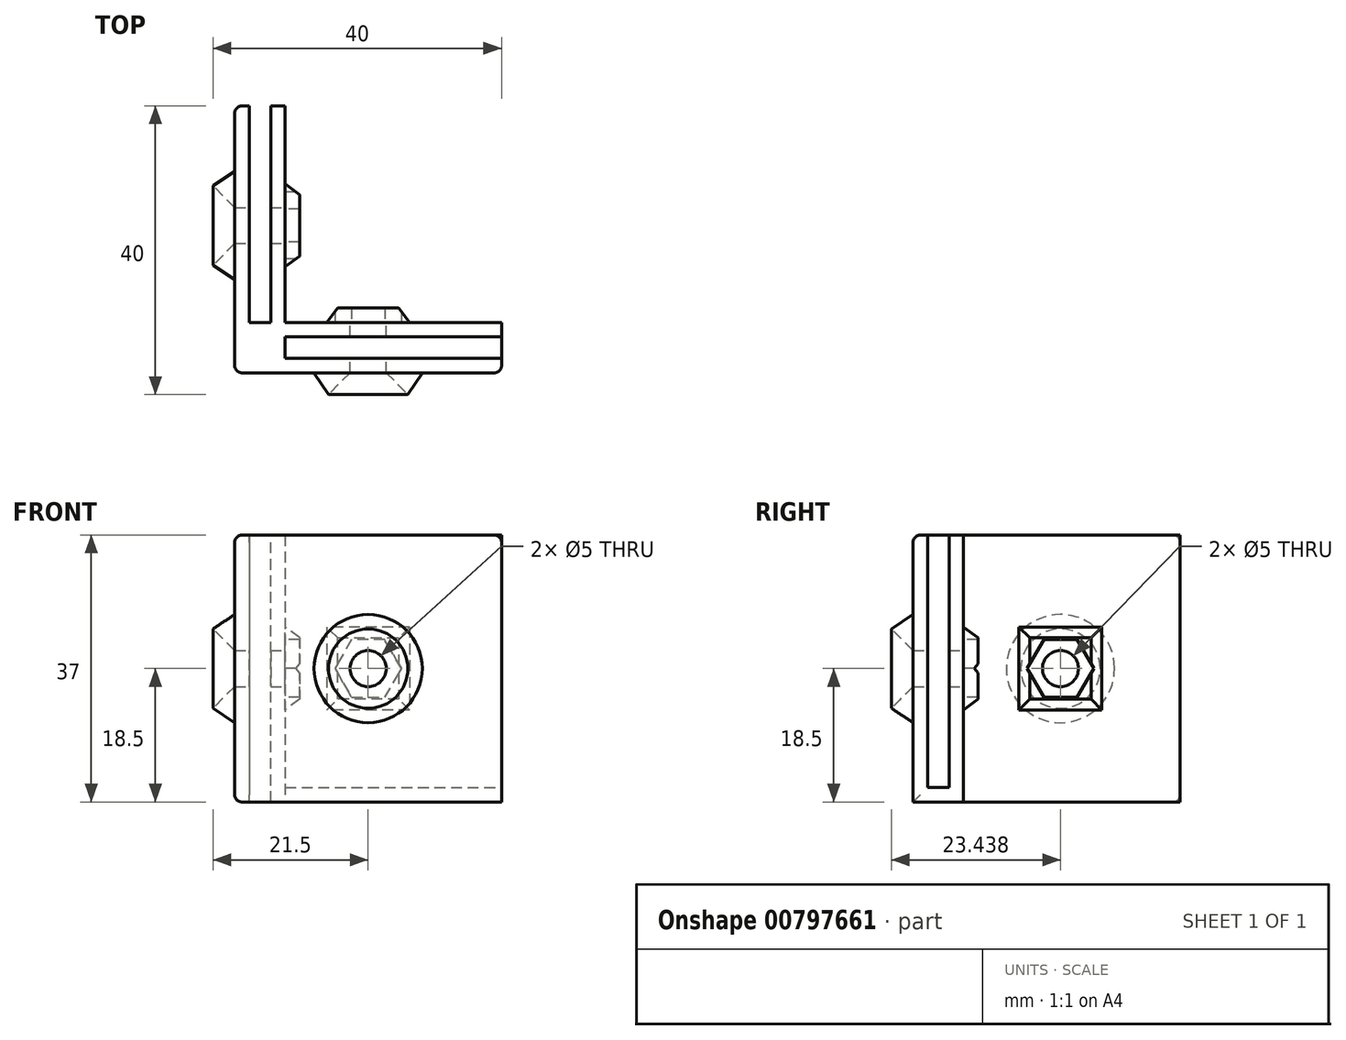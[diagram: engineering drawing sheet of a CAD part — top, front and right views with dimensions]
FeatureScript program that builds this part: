
annotation { "Feature Type Name" : "Feature", "Feature Type Description" : "" }
export const myFeature = defineFeature(function(context is Context, id is Id, definition is map)
    precondition{}
    {
        {
            var Q0;
            Q0=qCreatedBy(makeId("Front.planeOp"),FACE);
            var sketch = newSketch(context, id + "F0", { "sketchPlane" : qUnion([Q0])});
            skLineSegment(sketch, "E0.bottom", {"start": v(18.5, 18.5) * mm, "end": v(-18.5, 18.5) * mm});
            skLineSegment(sketch, "E0.top", {"start": v(18.5, -18.5) * mm, "end": v(-18.5, -18.5) * mm});
            skLineSegment(sketch, "E0.left", {"start": v(18.5, 18.5) * mm, "end": v(18.5, -18.5) * mm});
            skLineSegment(sketch, "E0.right", {"start": v(-18.5, 18.5) * mm, "end": v(-18.5, -18.5) * mm});
            skPoint(sketch, "E0.middle", {"position": v(0, 0) * mm});
            skSolve(sketch);
        }
        {
            var Q0;
            Q0=makeQuery(id+"F0.imprint","IMPRINT",FACE,{"disambiguationData":[TD([[makeQuery(id+"F0.imprint","IMPRINT",EDGE,{"derivedFrom":sQuery(id+"F0.wireOp",EDGE,"E0.bottom")}),1.0]])]});
            extrude(context, id + "F1", {"entities" : qUnion([Q0]), "depth" : 37 * mm, "offsetDistance" : 25 * mm});
        }
        {
            var Q0;
            Q0=makeQuery(id+"F1.opExtrude","CAP_FACE",FACE,{"disambiguationData":[OSD([sQuery(id+"F0.wireOp",EDGE,"E0.bottom"),sQuery(id+"F0.wireOp",EDGE,"E0.top"),sQuery(id+"F0.wireOp",EDGE,"E0.left"),sQuery(id+"F0.wireOp",EDGE,"E0.right")])],"isStart":true});
            var sketch = newSketch(context, id + "F2", { "sketchPlane" : qUnion([Q0])});
            skLineSegment(sketch, "E1", {"start": v(18.5, 18.5) * mm, "end": v(16.5, 18.5) * mm});
            skLineSegment(sketch, "E2", {"start": v(16.5, 18.5) * mm, "end": v(16.5, -16.5) * mm});
            skLineSegment(sketch, "E3", {"start": v(16.5, -16.5) * mm, "end": v(16.5, -18.5) * mm});
            skLineSegment(sketch, "E4", {"start": v(16.5, -18.5) * mm, "end": v(13.5, -18.5) * mm});
            skLineSegment(sketch, "E5", {"start": v(13.5, -18.5) * mm, "end": v(13.5, 18.5) * mm});
            skLineSegment(sketch, "E6", {"start": v(13.5, 18.5) * mm, "end": v(11.5, 18.5) * mm});
            skLineSegment(sketch, "E7", {"start": v(11.5, 18.5) * mm, "end": v(11.5, -18.5) * mm});
            skSolve(sketch);
        }
        {
            var Q0;
            Q0 = qSketchRegion(id + "F2", true);
            var Q1;
            {var subQ0=sQuery(id+"F2.wireOp",EDGE,"E7");Q1=makeQuery(id+"F2.imprint","IMPRINT",FACE,{"disambiguationData":[TD([[makeQuery(id+"F2.imprint","IMPRINT",EDGE,{"derivedFrom":subQ0}),-1.0]])]});}
            var Q2;
            {var subQ1=sQuery(id+"F2.wireOp",EDGE,"E2");Q2=makeQuery(id+"F2.imprint","IMPRINT",FACE,{"disambiguationData":[TD([[makeQuery(id+"F2.imprint","IMPRINT",EDGE,{"derivedFrom":subQ1}),-1.0]])]});}
            extrude(context, id + "F3", {"entities" : qUnion([Q0, Q1, Q2]), "operationType" : NewBodyOperationType.REMOVE, "oppositeDirection" : true, "depth" : 30 * mm, "offsetDistance" : 25 * mm});
        }
        {
            var Q0;
            Q0=makeQuery(id+"F1.opExtrude","SWEPT_FACE",FACE,{"disambiguationData":[OSD([sQuery(id+"F0.wireOp",EDGE,"E0.left")])]});
            var sketch = newSketch(context, id + "F4", { "sketchPlane" : qUnion([Q0])});
            skLineSegment(sketch, "E8", {"start": v(-37, 18.5) * mm, "end": v(-35, 18.5) * mm});
            skLineSegment(sketch, "E9", {"start": v(-35, 18.5) * mm, "end": v(-35, -16.5) * mm});
            skLineSegment(sketch, "E10", {"start": v(-35, -16.5) * mm, "end": v(-32, -16.5) * mm});
            skLineSegment(sketch, "E11", {"start": v(-32, -16.5) * mm, "end": v(-32, 18.5) * mm});
            skSolve(sketch);
        }
        {
            var Q0;
            Q0 = qSketchRegion(id + "F4", true);
            var Q1;
            {var subQ0=sQuery(id+"F4.wireOp",EDGE,"E9");Q1=makeQuery(id+"F4.imprint","IMPRINT",FACE,{"disambiguationData":[TD([[makeQuery(id+"F4.imprint","IMPRINT",EDGE,{"derivedFrom":subQ0}),1.0]])]});}
            extrude(context, id + "F5", {"entities" : qUnion([Q0, Q1]), "operationType" : NewBodyOperationType.REMOVE, "oppositeDirection" : true, "depth" : 30 * mm, "offsetDistance" : 25 * mm});
        }
        {
            var Q0;
            Q0=makeQuery(id+"F1.opExtrude","CAP_EDGE",EDGE,{"disambiguationData":[OSD([sQuery(id+"F0.wireOp",EDGE,"E0.right")])],"isStart":false});
            var Q1;
            Q1=makeQuery(id+"F1.opExtrude","SWEPT_EDGE",EDGE,{"disambiguationData":[OSD([sQuery(id+"F0.wireOp",EDGE,"E0.bottom"),sQuery(id+"F0.wireOp",EDGE,"E0.right")])]});
            var Q2;
            Q2=makeQuery(id+"F3.boolean.opBoolean","COPY",EDGE,{"derivedFrom":makeQuery(id+"F3.opExtrude","SWEPT_EDGE",EDGE,{"disambiguationData":[OSD([sQuery(id+"F0.wireOp",EDGE,"E0.bottom"),sQuery(id+"F2.wireOp",EDGE,"E6"),sQuery(id+"F2.wireOp",EDGE,"E7")])]})});
            var Q3;
            Q3=makeQuery(id+"F1.opExtrude","SWEPT_EDGE",EDGE,{"disambiguationData":[OSD([sQuery(id+"F0.wireOp",EDGE,"E0.top"),sQuery(id+"F0.wireOp",EDGE,"E0.right")])]});
            var Q4;
            Q4=makeQuery(id+"F3.boolean.opBoolean","COPY",EDGE,{"derivedFrom":makeQuery(id+"F3.opExtrude","SWEPT_EDGE",EDGE,{"disambiguationData":[OSD([sQuery(id+"F0.wireOp",EDGE,"E0.top"),sQuery(id+"F2.wireOp",EDGE,"E7")])]})});
            var Q5;
            Q5=makeQuery(id+"F1.opExtrude","CAP_EDGE",EDGE,{"disambiguationData":[OSD([sQuery(id+"F0.wireOp",EDGE,"E0.left")])],"isStart":false});
            var Q6;
            Q6=makeQuery(id+"F3.boolean.opBoolean","COPY",EDGE,{"derivedFrom":makeQuery(id+"F3.opExtrude","CAP_EDGE",EDGE,{"disambiguationData":[OSD([sQuery(id+"F0.wireOp",EDGE,"E0.left")])],"isStart":false})});
            fillet(context, id + "F6", {"entities" : qUnion([Q0, Q1, Q2, Q3, Q4, Q5, Q6]), "radius" : 1 * mm, "tangentPropagation" : true, "allowEdgeOverflow" : false});
        }
        {
            var Q0;
            Q0=makeQuery(id+"F3.boolean.opBoolean","COPY",FACE,{"derivedFrom":makeQuery(id+"F3.opExtrude","CAP_FACE",FACE,{"disambiguationData":[OSD([sQuery(id+"F0.wireOp",EDGE,"E0.bottom"),sQuery(id+"F0.wireOp",EDGE,"E0.top"),sQuery(id+"F0.wireOp",EDGE,"E0.left"),sQuery(id+"F2.wireOp",EDGE,"E7")])],"isStart":false})});
            var sketch = newSketch(context, id + "F7", { "sketchPlane" : qUnion([Q0])});
            skCircle(sketch, "E12", {"center": v(0, 0) * mm, "radius": 2.5 * mm});
            skLineSegment(sketch, "E13.bottom", {"start": v(-5.75, 5.75) * mm, "end": v(5.75, 5.75) * mm});
            skLineSegment(sketch, "E13.top", {"start": v(-5.75, -5.75) * mm, "end": v(5.75, -5.75) * mm});
            skLineSegment(sketch, "E13.left", {"start": v(-5.75, 5.75) * mm, "end": v(-5.75, -5.75) * mm});
            skLineSegment(sketch, "E13.right", {"start": v(5.75, 5.75) * mm, "end": v(5.75, -5.75) * mm});
            skCircle(sketch, "E14.cCircle", {"center": v(0, 0) * mm, "radius": 4 * mm, "construction": true});
            skPoint(sketch, "E14.cCircle.perimeterSnap0", {"position": v(0, 5.75) * mm});
            skLineSegment(sketch, "E14.0", {"start": v(-2.3, 4) * mm, "end": v(2.3, 4) * mm});
            skLineSegment(sketch, "E14.1", {"start": v(2.3, 4) * mm, "end": v(4.62, 0) * mm});
            skLineSegment(sketch, "E14.2", {"start": v(4.62, 0) * mm, "end": v(2.3, -4) * mm});
            skLineSegment(sketch, "E14.3", {"start": v(2.3, -4) * mm, "end": v(-2.3, -4) * mm});
            skLineSegment(sketch, "E14.4", {"start": v(-2.3, -4) * mm, "end": v(-4.62, 0) * mm});
            skLineSegment(sketch, "E14.5", {"start": v(-4.62, 0) * mm, "end": v(-2.3, 4) * mm});
            skPoint(sketch, "E14.0.midPoint", {"position": v(0, 4) * mm});
            skPoint(sketch, "E14.0.midPoint.positionSnap0", {"position": v(0, 5.75) * mm});
            skSolve(sketch);
        }
        {
            var Q0;
            Q0=makeQuery(id+"F7.imprint","IMPRINT",FACE,{"disambiguationData":[TD([[makeQuery(id+"F7.imprint","IMPRINT",EDGE,{"derivedFrom":sQuery(id+"F7.wireOp",EDGE,"E13.bottom")}),-1.0]])]});
            extrude(context, id + "F8", {"entities" : qUnion([Q0]), "operationType" : NewBodyOperationType.ADD, "depth" : 2 * mm, "offsetDistance" : 25 * mm});
        }
        {
            var Q0;
            Q0=makeQuery(id+"F7.imprint","IMPRINT",FACE,{"disambiguationData":[TD([[makeQuery(id+"F7.imprint","IMPRINT",EDGE,{"derivedFrom":sQuery(id+"F7.wireOp",EDGE,"E12")}),1.0]])]});
            extrude(context, id + "F9", {"entities" : qUnion([Q0]), "operationType" : NewBodyOperationType.REMOVE, "oppositeDirection" : true, "depth" : 25 * mm, "offsetDistance" : 25 * mm});
        }
        {
            var Q0;
            Q0=makeQuery(id+"F8.opExtrude","CAP_EDGE",EDGE,{"disambiguationData":[OSD([sQuery(id+"F7.wireOp",EDGE,"E13.left")])],"isStart":false});
            var Q1;
            Q1=makeQuery(id+"F8.opExtrude","CAP_EDGE",EDGE,{"disambiguationData":[OSD([sQuery(id+"F7.wireOp",EDGE,"E13.bottom")])],"isStart":false});
            var Q2;
            Q2=makeQuery(id+"F8.opExtrude","CAP_EDGE",EDGE,{"disambiguationData":[OSD([sQuery(id+"F7.wireOp",EDGE,"E13.right")])],"isStart":false});
            var Q3;
            Q3=makeQuery(id+"F8.opExtrude","CAP_EDGE",EDGE,{"disambiguationData":[OSD([sQuery(id+"F7.wireOp",EDGE,"E13.top")])],"isStart":false});
            chamfer(context, id + "F10", {"entities" : qUnion([Q0, Q1, Q2, Q3]), "chamferType" : ChamferType.TWO_OFFSETS, "width1" : 1.5 * mm, "oppositeDirection" : false, "width2" : 2 * mm, "tangentPropagation" : true});
        }
        {
            var Q0;
            Q0=makeQuery(id+"F1.opExtrude","CAP_FACE",FACE,{"disambiguationData":[OSD([sQuery(id+"F0.wireOp",EDGE,"E0.bottom"),sQuery(id+"F0.wireOp",EDGE,"E0.top"),sQuery(id+"F0.wireOp",EDGE,"E0.left"),sQuery(id+"F0.wireOp",EDGE,"E0.right")])],"isStart":false});
            var sketch = newSketch(context, id + "F11", { "sketchPlane" : qUnion([Q0])});
            skCircle(sketch, "E15", {"center": v(0, 0) * mm, "radius": 7.5 * mm});
            skSolve(sketch);
        }
        {
            var Q0;
            Q0=makeQuery(id+"F11.imprint","IMPRINT",FACE,{"disambiguationData":[TD([[makeQuery(id+"F11.imprint","IMPRINT",EDGE,{"derivedFrom":sQuery(id+"F11.wireOp",EDGE,"E15")}),1.0]])]});
            extrude(context, id + "F12", {"entities" : qUnion([Q0]), "operationType" : NewBodyOperationType.ADD, "depth" : 3 * mm, "offsetDistance" : 25 * mm});
        }
        {
            var Q0;
            Q0=makeQuery(id+"F12.opExtrude","CAP_EDGE",EDGE,{"disambiguationData":[OSD([sQuery(id+"F0.wireOp",EDGE,"E0.bottom"),sQuery(id+"F0.wireOp",EDGE,"E0.top"),sQuery(id+"F0.wireOp",EDGE,"E0.left"),sQuery(id+"F0.wireOp",EDGE,"E0.right"),sQuery(id+"F7.wireOp",EDGE,"E12")])],"isStart":false});
            chamfer(context, id + "F13", {"entities" : qUnion([Q0]), "width" : 3 * mm, "tangentPropagation" : true});
        }
        {
            var Q0;
            Q0=makeQuery(id+"F3.boolean.opBoolean","COPY",FACE,{"derivedFrom":makeQuery(id+"F3.opExtrude","SWEPT_FACE",FACE,{"disambiguationData":[OSD([sQuery(id+"F2.wireOp",EDGE,"E7")])]})});
            var sketch = newSketch(context, id + "F14", { "sketchPlane" : qUnion([Q0])});
            skCircle(sketch, "E16", {"center": v(-16.56, 0) * mm, "radius": 2.5 * mm});
            skCircle(sketch, "E17.cCircle", {"center": v(-16.56, 0) * mm, "radius": 4 * mm, "construction": true});
            skLineSegment(sketch, "E17.0", {"start": v(-18.87, 4) * mm, "end": v(-14.25, 4) * mm});
            skLineSegment(sketch, "E17.1", {"start": v(-14.25, 4) * mm, "end": v(-11.94, 0) * mm});
            skLineSegment(sketch, "E17.2", {"start": v(-11.94, 0) * mm, "end": v(-14.25, -4) * mm});
            skLineSegment(sketch, "E17.3", {"start": v(-14.25, -4) * mm, "end": v(-18.87, -4) * mm});
            skLineSegment(sketch, "E17.4", {"start": v(-18.87, -4) * mm, "end": v(-21.18, 0) * mm});
            skLineSegment(sketch, "E17.5", {"start": v(-21.18, 0) * mm, "end": v(-18.87, 4) * mm});
            skPoint(sketch, "E17.0.midPoint", {"position": v(-16.56, 4) * mm});
            skLineSegment(sketch, "E18.bottom", {"start": v(-22.31, -5.75) * mm, "end": v(-10.81, -5.75) * mm});
            skLineSegment(sketch, "E18.top", {"start": v(-22.31, 5.75) * mm, "end": v(-10.81, 5.75) * mm});
            skLineSegment(sketch, "E18.left", {"start": v(-22.31, -5.75) * mm, "end": v(-22.31, 5.75) * mm});
            skLineSegment(sketch, "E18.right", {"start": v(-10.81, -5.75) * mm, "end": v(-10.81, 5.75) * mm});
            skSolve(sketch);
        }
        {
            var Q0;
            Q0 = qSketchRegion(id + "F14", true);
            extrude(context, id + "F15", {"entities" : qUnion([Q0]), "operationType" : NewBodyOperationType.ADD, "depth" : 2 * mm, "offsetDistance" : 25 * mm});
        }
        {
            var Q0;
            Q0=makeQuery(id+"F14.imprint","IMPRINT",FACE,{"disambiguationData":[TD([[makeQuery(id+"F14.imprint","IMPRINT",EDGE,{"derivedFrom":sQuery(id+"F14.wireOp",EDGE,"E16")}),1.0]])]});
            extrude(context, id + "F16", {"entities" : qUnion([Q0]), "operationType" : NewBodyOperationType.REMOVE, "oppositeDirection" : true, "depth" : 25 * mm, "offsetDistance" : 25 * mm});
        }
        {
            var Q0;
            Q0=makeQuery(id+"F15.opExtrude","CAP_EDGE",EDGE,{"disambiguationData":[OSD([sQuery(id+"F14.wireOp",EDGE,"E18.right")])],"isStart":false});
            var Q1;
            Q1=makeQuery(id+"F15.opExtrude","CAP_EDGE",EDGE,{"disambiguationData":[OSD([sQuery(id+"F14.wireOp",EDGE,"E18.top")])],"isStart":false});
            var Q2;
            Q2=makeQuery(id+"F15.opExtrude","CAP_EDGE",EDGE,{"disambiguationData":[OSD([sQuery(id+"F14.wireOp",EDGE,"E18.bottom")])],"isStart":false});
            var Q3;
            Q3=makeQuery(id+"F15.opExtrude","CAP_EDGE",EDGE,{"disambiguationData":[OSD([sQuery(id+"F14.wireOp",EDGE,"E18.left")])],"isStart":false});
            chamfer(context, id + "F17", {"entities" : qUnion([Q0, Q1, Q2, Q3]), "chamferType" : ChamferType.TWO_OFFSETS, "width1" : 1.5 * mm, "oppositeDirection" : false, "width2" : 2 * mm, "tangentPropagation" : true});
        }
        {
            var Q0;
            Q0=makeQuery(id+"F1.opExtrude","SWEPT_FACE",FACE,{"disambiguationData":[OSD([sQuery(id+"F0.wireOp",EDGE,"E0.right")])]});
            var sketch = newSketch(context, id + "F18", { "sketchPlane" : qUnion([Q0])});
            skCircle(sketch, "E19", {"center": v(16.56, 0) * mm, "radius": 7.5 * mm});
            skSolve(sketch);
        }
        {
            var Q0;
            Q0=makeQuery(id+"F18.imprint","IMPRINT",FACE,{"disambiguationData":[TD([[makeQuery(id+"F18.imprint","IMPRINT",EDGE,{"derivedFrom":sQuery(id+"F18.wireOp",EDGE,"E19")}),1.0]])]});
            extrude(context, id + "F19", {"entities" : qUnion([Q0]), "operationType" : NewBodyOperationType.ADD, "depth" : 3 * mm, "offsetDistance" : 25 * mm});
        }
        {
            var Q0;
            Q0=makeQuery(id+"F19.opExtrude","CAP_EDGE",EDGE,{"disambiguationData":[OSD([sQuery(id+"F0.wireOp",EDGE,"E0.right"),sQuery(id+"F14.wireOp",EDGE,"E16")])],"isStart":false});
            chamfer(context, id + "F20", {"entities" : qUnion([Q0]), "width" : 3 * mm, "tangentPropagation" : true});
        }
        {
            var Q0;
            Q0=makeQuery(id+"F19.opExtrude","CAP_EDGE",EDGE,{"disambiguationData":[OSD([sQuery(id+"F18.wireOp",EDGE,"E19")])],"isStart":false});
            var Q1;
            Q1=makeQuery(id+"F12.opExtrude","CAP_EDGE",EDGE,{"disambiguationData":[OSD([sQuery(id+"F11.wireOp",EDGE,"E15")])],"isStart":false});
            chamfer(context, id + "F21", {"entities" : qUnion([Q0, Q1]), "chamferType" : ChamferType.TWO_OFFSETS, "width1" : 2 * mm, "oppositeDirection" : false, "width2" : 3 * mm, "tangentPropagation" : true});
        }
        {
            var Q0;
            Q0=makeQuery(id+"F1.opExtrude","CAP_EDGE",EDGE,{"disambiguationData":[OSD([sQuery(id+"F0.wireOp",EDGE,"E0.bottom")])],"isStart":false});
            var Q1;
            {var subQ0=sQuery(id+"F0.wireOp",EDGE,"E0.bottom");var subQ1=makeQuery(id+"F1.opExtrude","CAP_EDGE",EDGE,{"disambiguationData":[OSD([subQ0])],"isStart":true});Q1=makeQuery(id+"F3.boolean.opBoolean","COPY",EDGE,{"derivedFrom":makeQuery(id+"F3.opExtrude","CAP_EDGE",EDGE,{"disambiguationData":[OSD([subQ0]),TDD([makeQuery(id+"F2.imprint","IMPRINT",EDGE,{"disambiguationData":[TD([[makeQuery(id+"F2.imprint","INTERSECT",VERTEX,{"derivedFrom":[subQ1,makeQuery(id+"F1.opExtrude","CAP_EDGE",EDGE,{"disambiguationData":[OSD([sQuery(id+"F0.wireOp",EDGE,"E0.left")])],"isStart":true})]}),-1.0]])],"derivedFrom":subQ1})])],"isStart":false})});}
            var Q2;
            Q2=makeQuery(id+"F3.boolean.opBoolean","COPY",EDGE,{"derivedFrom":makeQuery(id+"F3.opExtrude","CAP_EDGE",EDGE,{"disambiguationData":[OSD([sQuery(id+"F2.wireOp",EDGE,"E7")])],"isStart":true})});
            var Q3;
            Q3=makeQuery(id+"F1.opExtrude","CAP_EDGE",EDGE,{"disambiguationData":[OSD([sQuery(id+"F0.wireOp",EDGE,"E0.right")])],"isStart":true});
            fillet(context, id + "F22", {"entities" : qUnion([Q0, Q1, Q2, Q3]), "radius" : 1 * mm, "tangentPropagation" : true, "allowEdgeOverflow" : false});
        }
    });
